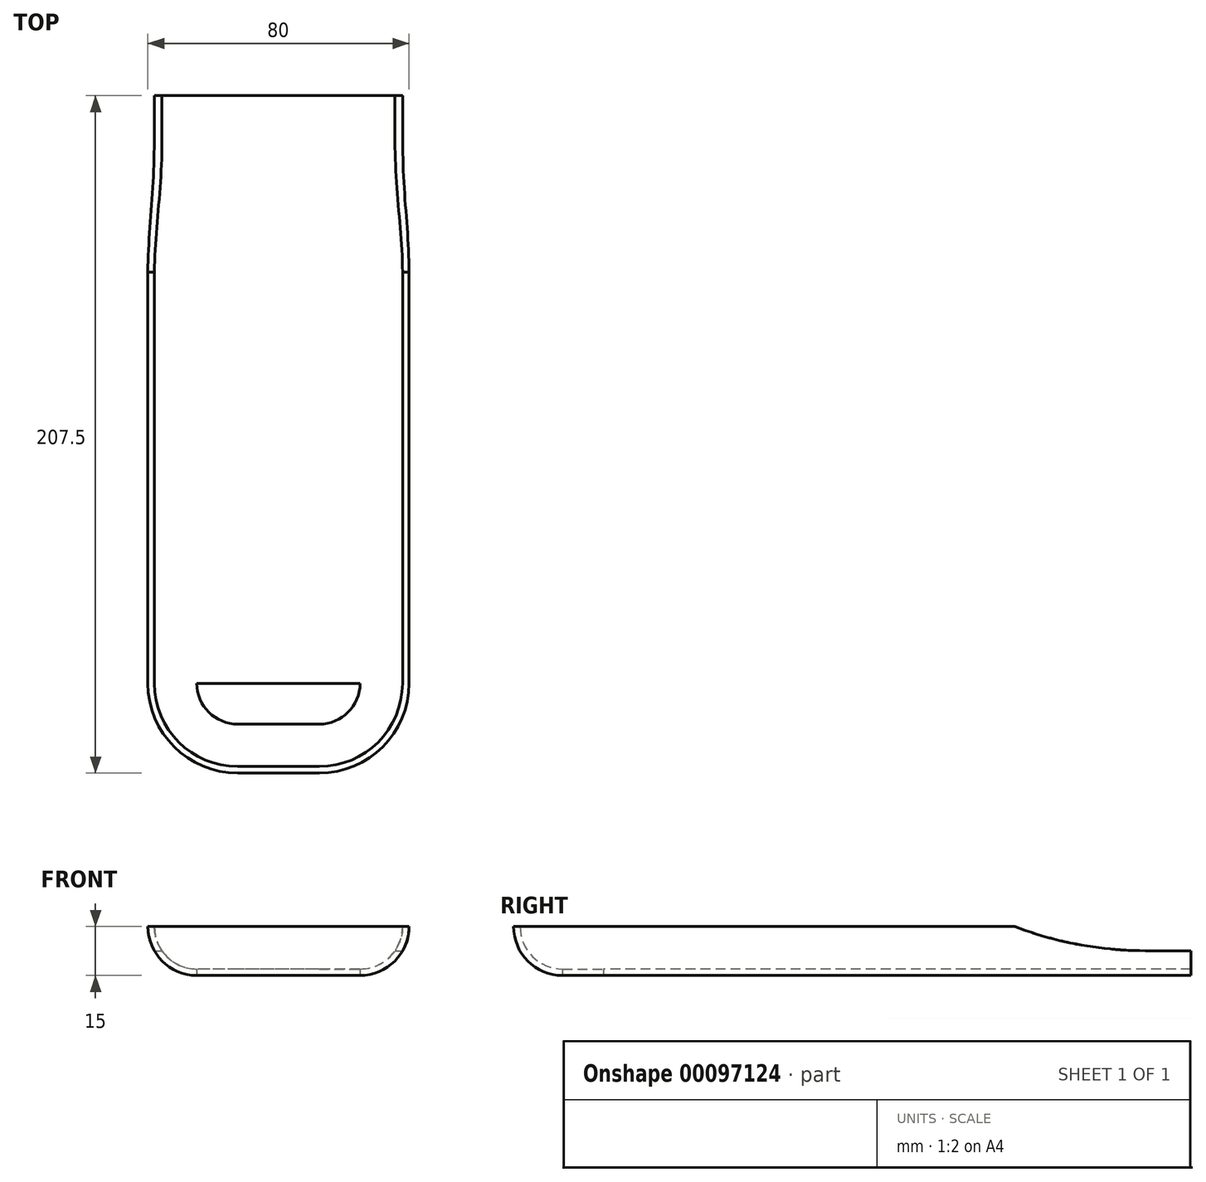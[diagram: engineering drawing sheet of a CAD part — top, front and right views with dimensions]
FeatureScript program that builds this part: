
annotation { "Feature Type Name" : "Feature", "Feature Type Description" : "" }
export const myFeature = defineFeature(function(context is Context, id is Id, definition is map)
    precondition{}
    {
        {
            var Q0;
            Q0=qCreatedBy(makeId("Top.planeOp"),FACE);
            var sketch = newSketch(context, id + "F0", { "sketchPlane" : qUnion([Q0])});
            skLineSegment(sketch, "E0.bottom", {"start": v(40, 90) * mm, "end": v(-40, 90) * mm});
            skLineSegment(sketch, "E0.top", {"start": v(40, -90) * mm, "end": v(-40, -90) * mm});
            skLineSegment(sketch, "E0.left", {"start": v(40, 90) * mm, "end": v(40, -90) * mm});
            skLineSegment(sketch, "E0.right", {"start": v(-40, 90) * mm, "end": v(-40, -90) * mm});
            skPoint(sketch, "E0.middle", {"position": v(0, 0) * mm});
            skSolve(sketch);
        }
        {
            var Q0;
            Q0=makeQuery(id+"F0.imprint","IMPRINT",FACE,{"disambiguationData":[TD([[makeQuery(id+"F0.imprint","IMPRINT",EDGE,{"derivedFrom":sQuery(id+"F0.wireOp",EDGE,"E0.bottom")}),1.0]])]});
            extrude(context, id + "F1", {"entities" : qUnion([Q0]), "depth" : 15 * mm});
        }
        {
            var Q0;
            Q0=makeQuery(id+"F1.opExtrude","SWEPT_FACE",FACE,{"disambiguationData":[OSD([sQuery(id+"F0.wireOp",EDGE,"E0.top")])]});
            var sketch = newSketch(context, id + "F2", { "sketchPlane" : qUnion([Q0])});
            skArc(sketch, "E1", {"start": v(-40, 15) * mm, "mid": v(-35.6, 4.4) * mm, "end": v(-25, 0) * mm});
            skArc(sketch, "E2", {"start": v(-38, 15) * mm, "mid": v(-34.2, 5.8) * mm, "end": v(-25, 2) * mm});
            skArc(sketch, "E3", {"start": v(25, 0) * mm, "mid": v(35.6, 4.4) * mm, "end": v(40, 15) * mm});
            skArc(sketch, "E4", {"start": v(25, 2) * mm, "mid": v(34.2, 5.8) * mm, "end": v(38, 15) * mm});
            skLineSegment(sketch, "E5", {"start": v(-25, 2) * mm, "end": v(-25, 0) * mm, "construction": true});
            skLineSegment(sketch, "E6", {"start": v(25, 2) * mm, "end": v(25, 0) * mm, "construction": true});
            skLineSegment(sketch, "E7", {"start": v(-40, 15) * mm, "end": v(-38, 15) * mm, "construction": true});
            skLineSegment(sketch, "E8", {"start": v(38, 15) * mm, "end": v(40, 15) * mm, "construction": true});
            skLineSegment(sketch, "E9", {"start": v(35.6, 4.4) * mm, "end": v(34.2, 5.8) * mm, "construction": true});
            skLineSegment(sketch, "E10", {"start": v(-34.2, 5.8) * mm, "end": v(-35.6, 4.4) * mm, "construction": true});
            skLineSegment(sketch, "E11.bottom", {"start": v(-25, 2) * mm, "end": v(25, 2) * mm});
            skLineSegment(sketch, "E11.top", {"start": v(-25, 0) * mm, "end": v(25, 0) * mm});
            skLineSegment(sketch, "E11.left", {"start": v(-25, 2) * mm, "end": v(-25, 0) * mm});
            skLineSegment(sketch, "E11.right", {"start": v(25, 2) * mm, "end": v(25, 0) * mm});
            skLineSegment(sketch, "E12", {"start": v(-12.5, 15) * mm, "end": v(-12.5, 2) * mm, "construction": true});
            skLineSegment(sketch, "E13", {"start": v(12.5, 15) * mm, "end": v(12.5, 2) * mm, "construction": true});
            skLineSegment(sketch, "E14", {"start": v(-12.5, 8.5) * mm, "end": v(12.5, 8.5) * mm, "construction": true});
            skPoint(sketch, "E15", {"position": v(0, 8.5) * mm});
            skPoint(sketch, "E16", {"position": v(0, 15) * mm});
            skSolve(sketch);
        }
        {
            var Q0;
            {var subQ0=sQuery(id+"F2.wireOp",EDGE,"E1");Q0=makeQuery(id+"F2.imprint","IMPRINT",FACE,{"disambiguationData":[TD([[makeQuery(id+"F2.imprint","IMPRINT",EDGE,{"derivedFrom":subQ0}),1.0]])]});}
            var Q1;
            Q1=makeQuery(id+"F2.imprint","IMPRINT",FACE,{"disambiguationData":[TD([[makeQuery(id+"F2.imprint","IMPRINT",EDGE,{"derivedFrom":sQuery(id+"F2.wireOp",EDGE,"E11.bottom")}),-1.0]])]});
            var Q2;
            {var subQ0=sQuery(id+"F2.wireOp",EDGE,"E3");Q2=makeQuery(id+"F2.imprint","IMPRINT",FACE,{"disambiguationData":[TD([[makeQuery(id+"F2.imprint","IMPRINT",EDGE,{"derivedFrom":subQ0}),1.0]])]});}
            var Q3;
            Q3=makeQuery(id+"F1.opExtrude","SWEPT_FACE",FACE,{"disambiguationData":[OSD([sQuery(id+"F0.wireOp",EDGE,"E0.bottom")])]});
            extrude(context, id + "F3", {"entities" : qUnion([Q0, Q1, Q2]), "operationType" : NewBodyOperationType.INTERSECT, "endBound" : BoundingType.UP_TO_SURFACE, "oppositeDirection" : true, "endBoundEntityFace" : qUnion([Q3]), "depth" : 25 * mm});
        }
        {
            var Q0;
            {var subQ0=sQuery(id+"F2.wireOp",EDGE,"E3");Q0=makeQuery(id+"F2.imprint","IMPRINT",FACE,{"disambiguationData":[TD([[makeQuery(id+"F2.imprint","IMPRINT",EDGE,{"derivedFrom":subQ0}),1.0]])]});}
            var Q1;
            Q1=sQuery(id+"F2.wireOp",EDGE,"E13");
            revolve(context, id + "F4", {"operationType" : NewBodyOperationType.ADD, "entities" : qUnion([Q0]), "axis" : qUnion([Q1]), "revolveType" : RevolveType.ONE_DIRECTION, "angle" : 90 * degree});
        }
        {
            var Q0;
            {var subQ0=sQuery(id+"F2.wireOp",EDGE,"E1");Q0=makeQuery(id+"F2.imprint","IMPRINT",FACE,{"disambiguationData":[TD([[makeQuery(id+"F2.imprint","IMPRINT",EDGE,{"derivedFrom":subQ0}),1.0]])]});}
            var Q1;
            Q1=sQuery(id+"F2.wireOp",EDGE,"E12");
            revolve(context, id + "F5", {"operationType" : NewBodyOperationType.ADD, "entities" : qUnion([Q0]), "axis" : qUnion([Q1]), "revolveType" : RevolveType.ONE_DIRECTION, "oppositeDirection" : true, "angle" : 90 * degree});
        }
        {
            var Q0;
            Q0=makeQuery(id+"F5.opRevolve","CAP_FACE",FACE,{"disambiguationData":[OSD([sQuery(id+"F0.wireOp",EDGE,"E0.top"),sQuery(id+"F2.wireOp",EDGE,"E1"),sQuery(id+"F2.wireOp",EDGE,"E2"),sQuery(id+"F2.wireOp",EDGE,"E11.left")])],"isStart":false});
            var Q1;
            Q1=makeQuery(id+"F4.opRevolve","CAP_FACE",FACE,{"disambiguationData":[OSD([sQuery(id+"F0.wireOp",EDGE,"E0.top"),sQuery(id+"F2.wireOp",EDGE,"E3"),sQuery(id+"F2.wireOp",EDGE,"E4"),sQuery(id+"F2.wireOp",EDGE,"E11.right")])],"isStart":false});
            extrude(context, id + "F6", {"entities" : qUnion([Q0]), "operationType" : NewBodyOperationType.ADD, "endBound" : BoundingType.UP_TO_SURFACE, "endBoundEntityFace" : qUnion([Q1]), "depth" : 25 * mm});
        }
        {
            var Q0;
            {var subQ0=sQuery(id+"F0.wireOp",EDGE,"E0.left");Q0=makeQuery(id+"F3.boolean.opBoolean","MERGE",EDGE,{"derivedFrom":[makeQuery(id+"F1.opExtrude","CAP_EDGE",EDGE,{"disambiguationData":[OSD([subQ0])],"isStart":false}),makeQuery(id+"F3.boolean.toolComplement.opBoolean","COPY",EDGE,{"derivedFrom":makeQuery(id+"F3.opExtrude","SWEPT_EDGE",EDGE,{"disambiguationData":[OSD([sQuery(id+"F0.wireOp",EDGE,"E0.top"),subQ0,sQuery(id+"F2.wireOp",EDGE,"E3")])]})})]});}
            cPlane(context, id + "F7", {"entities" : qUnion([Q0]), "cplaneType" : CPlaneType.LINE_ANGLE, "offset" : 150 * mm, "angle" : 90 * degree, "width" : 150 * mm, "height" : 150 * mm});
        }
        {
            var Q0;
            Q0=qCreatedBy(id+"F7.planeOp",FACE);
            var sketch = newSketch(context, id + "F8", { "sketchPlane" : qUnion([Q0])});
            skLineSegment(sketch, "E17.0", {"start": v(90, 15) * mm, "end": v(-90, 15) * mm});
            skLineSegment(sketch, "E18.0", {"start": v(90, 0) * mm, "end": v(-90, 0) * mm});
            skArc(sketch, "E19", {"start": v(36, 15) * mm, "mid": v(55.66, 9.47) * mm, "end": v(76, 7.6) * mm});
            skLineSegment(sketch, "E20", {"start": v(76, 7.6) * mm, "end": v(90, 7.6) * mm});
            skLineSegment(sketch, "E21.0", {"start": v(90, 15) * mm, "end": v(90, 0) * mm});
            skSolve(sketch);
        }
        {
            var Q0;
            {var subQ3=sQuery(id+"F8.wireOp",EDGE,"E19");Q0=makeQuery(id+"F8.imprint","IMPRINT",FACE,{"disambiguationData":[TD([[makeQuery(id+"F8.imprint","IMPRINT",EDGE,{"derivedFrom":subQ3}),1.0]])]});}
            var Q1;
            Q1=makeQuery(id+"F3.boolean.opBoolean","COPY",FACE,{"derivedFrom":makeQuery(id+"F3.boolean.toolComplement.opBoolean","COPY",FACE,{"derivedFrom":makeQuery(id+"F3.opExtrude","SWEPT_FACE",FACE,{"disambiguationData":[OSD([sQuery(id+"F2.wireOp",EDGE,"E1")])]})})});
            extrude(context, id + "F9", {"entities" : qUnion([Q0]), "operationType" : NewBodyOperationType.REMOVE, "endBound" : BoundingType.THROUGH_ALL, "oppositeDirection" : true, "endBoundEntityFace" : qUnion([Q1]), "depth" : 25 * mm});
        }
    });
